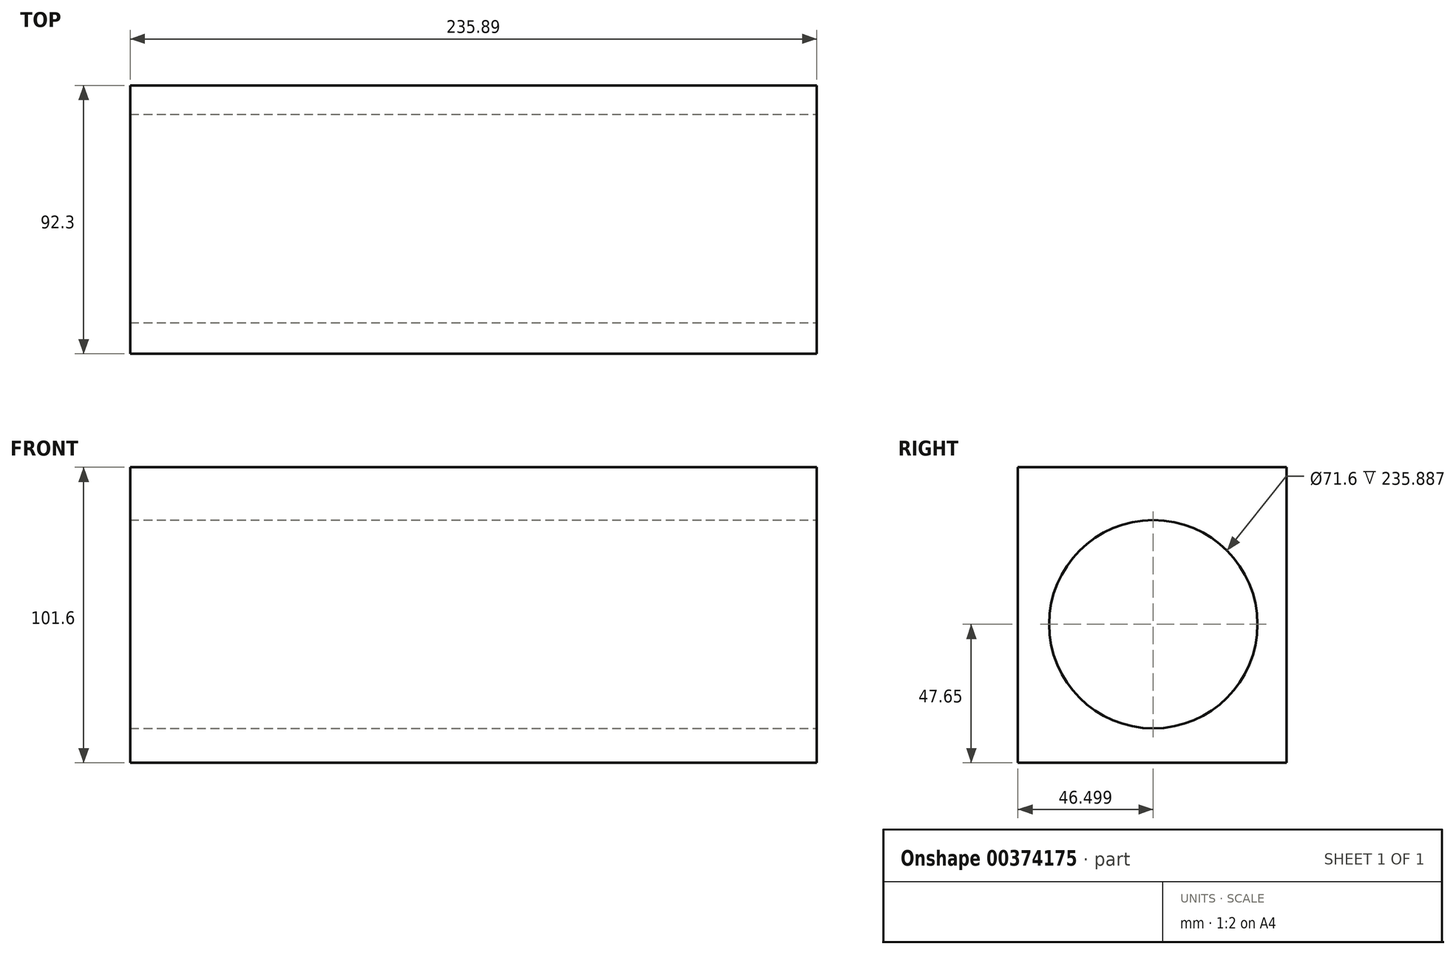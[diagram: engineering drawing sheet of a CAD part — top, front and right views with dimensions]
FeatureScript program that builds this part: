
annotation { "Feature Type Name" : "Feature", "Feature Type Description" : "" }
export const myFeature = defineFeature(function(context is Context, id is Id, definition is map)
    precondition{}
    {
        {
            var Q0;
            Q0=qCreatedBy(makeId("Top.planeOp"),FACE);
            var sketch = newSketch(context, id + "F0", { "sketchPlane" : qUnion([Q0])});
            skLineSegment(sketch, "E0.bottom", {"start": v(-111.55, 31.4) * mm, "end": v(124.34, 31.4) * mm});
            skLineSegment(sketch, "E0.top", {"start": v(-111.55, -60.9) * mm, "end": v(124.34, -60.9) * mm});
            skLineSegment(sketch, "E0.left", {"start": v(-111.55, 31.4) * mm, "end": v(-111.55, -60.9) * mm});
            skLineSegment(sketch, "E0.right", {"start": v(124.34, 31.4) * mm, "end": v(124.34, -60.9) * mm});
            skSolve(sketch);
        }
        {
            var Q0;
            Q0=makeQuery(id+"F0.imprint","IMPRINT",FACE,{"disambiguationData":[TD([[makeQuery(id+"F0.imprint","IMPRINT",EDGE,{"derivedFrom":sQuery(id+"F0.wireOp",EDGE,"E0.bottom")}),-1.0]])]});
            extrude(context, id + "F1", {"entities" : qUnion([Q0]), "offsetDistance" : 25.4 * mm, "depth" : 101.6 * mm});
        }
        {
            var Q0;
            Q0=makeQuery(id+"F1.opExtrude","SWEPT_FACE",FACE,{"disambiguationData":[OSD([sQuery(id+"F0.wireOp",EDGE,"E0.right")])]});
            var sketch = newSketch(context, id + "F2", { "sketchPlane" : qUnion([Q0])});
            skCircle(sketch, "E1", {"center": v(-14.4, 47.65) * mm, "radius": 35.8 * mm});
            skSolve(sketch);
        }
        {
            var Q0;
            Q0=makeQuery(id+"F2.imprint","IMPRINT",FACE,{"disambiguationData":[TD([[makeQuery(id+"F2.imprint","IMPRINT",EDGE,{"derivedFrom":sQuery(id+"F2.wireOp",EDGE,"E1")}),1.0]])]});
            extrude(context, id + "F3", {"entities" : qUnion([Q0]), "operationType" : NewBodyOperationType.REMOVE, "oppositeDirection" : true, "depth" : 281.43 * mm});
        }
    });
